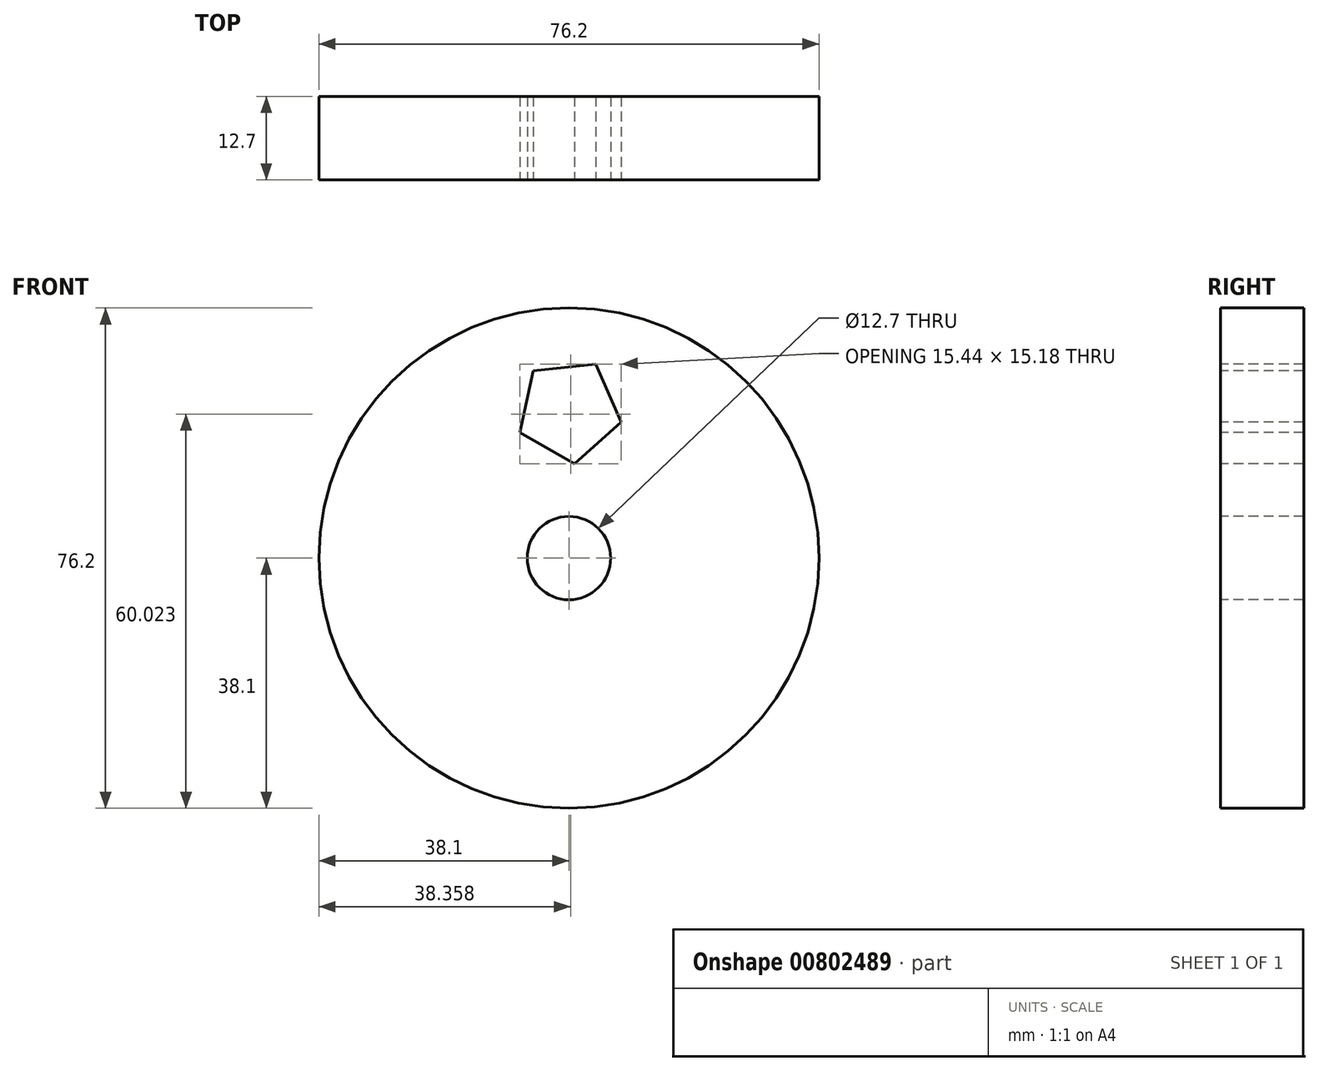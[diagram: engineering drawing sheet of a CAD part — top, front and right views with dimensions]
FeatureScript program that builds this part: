
annotation { "Feature Type Name" : "Feature", "Feature Type Description" : "" }
export const myFeature = defineFeature(function(context is Context, id is Id, definition is map)
    precondition{}
    {
        {
            var Q0;
            Q0=qCreatedBy(makeId("Front.planeOp"),FACE);
            var sketch = newSketch(context, id + "F0", { "sketchPlane" : qUnion([Q0])});
            skCircle(sketch, "E0", {"center": v(0, 0) * mm, "radius": 38.1 * mm});
            skSolve(sketch);
        }
        {
            var Q0;
            Q0=qSketchRegion(id+"F0",true);
            extrude(context, id + "F1", {"entities" : qUnion([Q0]), "depth" : 12.7 * mm, "offsetDistance" : 25.4 * mm});
        }
        {
            var Q0;
            Q0=makeQuery(id+"F1.opExtrude","CAP_FACE",FACE,{"disambiguationData":[OSD([sQuery(id+"F0.wireOp",EDGE,"E0")])],"isStart":false});
            var sketch = newSketch(context, id + "F2", { "sketchPlane" : qUnion([Q0])});
            skCircle(sketch, "E1", {"center": v(0, 0) * mm, "radius": 6.35 * mm});
            skSolve(sketch);
        }
        {
            var Q0;
            Q0=qSketchRegion(id+"F2",true);
            extrude(context, id + "F3", {"entities" : qUnion([Q0]), "operationType" : NewBodyOperationType.REMOVE, "endBound" : BoundingType.THROUGH_ALL, "oppositeDirection" : true, "depth" : 25.4 * mm, "offsetDistance" : 25.4 * mm});
        }
        {
            var Q0;
            Q0=makeQuery(id+"F1.opExtrude","CAP_FACE",FACE,{"disambiguationData":[OSD([sQuery(id+"F0.wireOp",EDGE,"E0")])],"isStart":false});
            var sketch = newSketch(context, id + "F4", { "sketchPlane" : qUnion([Q0])});
            skCircle(sketch, "E2.cCircle", {"center": v(0, 22.45) * mm, "radius": 6.6 * mm, "construction": true});
            skLineSegment(sketch, "E2.0", {"start": v(7.98, 20.74) * mm, "end": v(0.84, 14.34) * mm});
            skLineSegment(sketch, "E2.1", {"start": v(0.84, 14.34) * mm, "end": v(-7.46, 19.15) * mm});
            skLineSegment(sketch, "E2.2", {"start": v(-7.46, 19.15) * mm, "end": v(-5.45, 28.53) * mm});
            skLineSegment(sketch, "E2.3", {"start": v(-5.45, 28.53) * mm, "end": v(4.1, 29.51) * mm});
            skLineSegment(sketch, "E2.4", {"start": v(4.1, 29.51) * mm, "end": v(7.98, 20.74) * mm});
            skPoint(sketch, "E2.0.midPoint", {"position": v(4.4, 17.54) * mm});
            skSolve(sketch);
        }
        {
            var Q0;
            Q0 = qSketchRegion(id + "F4", true);
            extrude(context, id + "F5", {"entities" : qUnion([Q0]), "operationType" : NewBodyOperationType.REMOVE, "endBound" : BoundingType.THROUGH_ALL, "oppositeDirection" : true, "depth" : 25.4 * mm, "offsetDistance" : 25.4 * mm});
        }
    });
